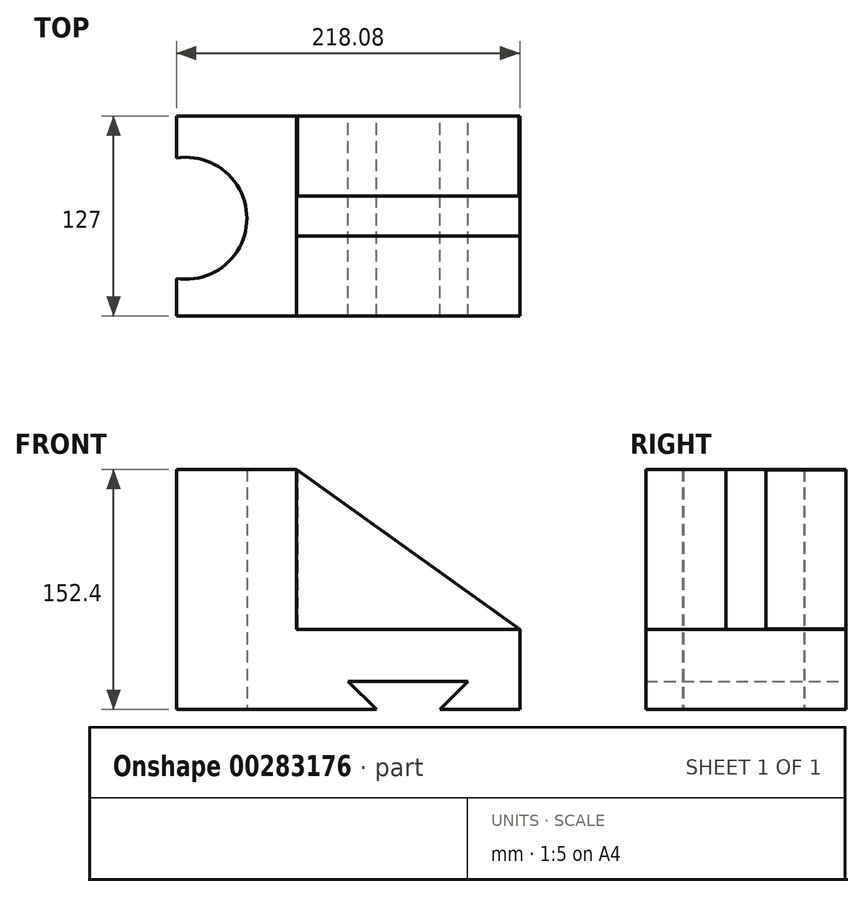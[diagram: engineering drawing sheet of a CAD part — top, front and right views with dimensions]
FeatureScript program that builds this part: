
annotation { "Feature Type Name" : "Feature", "Feature Type Description" : "" }
export const myFeature = defineFeature(function(context is Context, id is Id, definition is map)
    precondition{}
    {
        {
            var Q0;
            Q0=qCreatedBy(makeId("Front.planeOp"),FACE);
            var sketch = newSketch(context, id + "F0", { "sketchPlane" : qUnion([Q0])});
            skLineSegment(sketch, "E0", {"start": v(-163.44, 77.73) * mm, "end": v(-239.64, 77.73) * mm});
            skLineSegment(sketch, "E1", {"start": v(-239.64, 77.73) * mm, "end": v(-239.64, -74.67) * mm});
            skLineSegment(sketch, "E2", {"start": v(-239.64, -74.67) * mm, "end": v(-112.64, -74.67) * mm});
            skLineSegment(sketch, "E3", {"start": v(-112.64, -74.67) * mm, "end": v(-130.6, -56.7) * mm});
            skLineSegment(sketch, "E4", {"start": v(-130.6, -56.7) * mm, "end": v(-54.4, -56.7) * mm});
            skLineSegment(sketch, "E5", {"start": v(-54.4, -56.7) * mm, "end": v(-72.36, -74.67) * mm});
            skLineSegment(sketch, "E6", {"start": v(-72.36, -74.67) * mm, "end": v(-21.56, -74.67) * mm});
            skLineSegment(sketch, "E7", {"start": v(-21.56, -74.67) * mm, "end": v(-21.56, -23.87) * mm});
            skLineSegment(sketch, "E8", {"start": v(-21.56, -23.87) * mm, "end": v(-163.8, -23.87) * mm});
            skLineSegment(sketch, "E9", {"start": v(-163.8, -23.87) * mm, "end": v(-163.44, 77.73) * mm});
            skLineSegment(sketch, "E10", {"start": v(-163.44, 77.73) * mm, "end": v(-21.56, -23.87) * mm});
            skSolve(sketch);
        }
        {
            var Q0;
            Q0=makeQuery(id+"F0.imprint","IMPRINT",FACE,{"disambiguationData":[TD([[makeQuery(id+"F0.imprint","IMPRINT",EDGE,{"derivedFrom":sQuery(id+"F0.wireOp",EDGE,"E0")}),1.0]])]});
            extrude(context, id + "F1", {"entities" : qUnion([Q0]), "depth" : 127 * mm});
        }
        {
            var Q0;
            Q0=qCreatedBy(makeId("Top.planeOp"),FACE);
            var sketch = newSketch(context, id + "F2", { "sketchPlane" : qUnion([Q0])});
            skCircle(sketch, "E11", {"center": v(-233.67, -64.92) * mm, "radius": 38.73 * mm});
            skPoint(sketch, "E11.first.point", {"position": v(-239.98, -26.7) * mm});
            skPoint(sketch, "E11.second.point", {"position": v(-195, -66.9) * mm});
            skPoint(sketch, "E11.third.point", {"position": v(-239.98, -103.13) * mm});
            skSolve(sketch);
        }
        {
            var Q0;
            Q0 = qSketchRegion(id + "F2", true);
            extrude(context, id + "F3", {"entities" : qUnion([Q0]), "operationType" : NewBodyOperationType.REMOVE, "depth" : 127 * mm});
        }
        {
            var Q0;
            Q0=makeQuery(id+"F3.boolean.opBoolean","COPY",FACE,{"derivedFrom":makeQuery(id+"F3.opExtrude","CAP_FACE",FACE,{"disambiguationData":[OSD([sQuery(id+"F2.wireOp",EDGE,"E11")])],"isStart":true})});
            extrude(context, id + "F4", {"entities" : qUnion([Q0]), "operationType" : NewBodyOperationType.REMOVE, "oppositeDirection" : true, "depth" : 127 * mm});
        }
        {
            var Q0;
            Q0=makeQuery(id+"F0.imprint","IMPRINT",FACE,{"disambiguationData":[TD([[makeQuery(id+"F0.imprint","IMPRINT",EDGE,{"derivedFrom":sQuery(id+"F0.wireOp",EDGE,"E8")}),-1.0]])]});
            extrude(context, id + "F5", {"entities" : qUnion([Q0]), "operationType" : NewBodyOperationType.ADD, "depth" : 127 * mm});
        }
        {
            var Q0;
            {var subQ0=sQuery(id+"F0.wireOp",EDGE,"E9");var subQ1=sQuery(id+"F0.wireOp",EDGE,"E8");Q0=makeQuery(id+"F5.boolean.opBoolean","MERGE",FACE,{"derivedFrom":[makeQuery(id+"F1.opExtrude","CAP_FACE",FACE,{"disambiguationData":[OSD([sQuery(id+"F0.wireOp",EDGE,"E0"),sQuery(id+"F0.wireOp",EDGE,"E1"),sQuery(id+"F0.wireOp",EDGE,"E2"),sQuery(id+"F0.wireOp",EDGE,"E3"),sQuery(id+"F0.wireOp",EDGE,"E4"),sQuery(id+"F0.wireOp",EDGE,"E5"),sQuery(id+"F0.wireOp",EDGE,"E6"),sQuery(id+"F0.wireOp",EDGE,"E7"),subQ1,subQ0])],"isStart":false}),makeQuery(id+"F5.opExtrude","CAP_FACE",FACE,{"disambiguationData":[OSD([subQ1,subQ0,sQuery(id+"F0.wireOp",EDGE,"E10")])],"isStart":false})]});}
            var sketch = newSketch(context, id + "F6", { "sketchPlane" : qUnion([Q0])});
            skLineSegment(sketch, "E12", {"start": v(-163.44, 77.73) * mm, "end": v(-163.44, -23.87) * mm});
            skLineSegment(sketch, "E13", {"start": v(-163.44, -23.87) * mm, "end": v(-21.56, -23.87) * mm});
            skLineSegment(sketch, "E14", {"start": v(-21.56, -23.87) * mm, "end": v(-163.44, 77.73) * mm});
            skSolve(sketch);
        }
        {
            var Q0;
            Q0=makeQuery(id+"F6.imprint","IMPRINT",FACE,{"disambiguationData":[TD([[makeQuery(id+"F6.imprint","IMPRINT",EDGE,{"derivedFrom":sQuery(id+"F6.wireOp",EDGE,"E12")}),1.0]])]});
            extrude(context, id + "F7", {"entities" : qUnion([Q0]), "operationType" : NewBodyOperationType.REMOVE, "oppositeDirection" : true, "depth" : 50.8 * mm});
        }
        {
            var Q0;
            Q0=makeQuery(id+"F0.imprint","IMPRINT",FACE,{"disambiguationData":[TD([[makeQuery(id+"F0.imprint","IMPRINT",EDGE,{"derivedFrom":sQuery(id+"F0.wireOp",EDGE,"E0")}),1.0]])]});
            var sketch = newSketch(context, id + "F8", { "sketchPlane" : qUnion([Q0])});
            skLineSegment(sketch, "E15", {"start": v(-20.42, -23.5) * mm, "end": v(-162.88, 78.05) * mm});
            skLineSegment(sketch, "E16", {"start": v(-162.88, 78.05) * mm, "end": v(-162.88, -23.5) * mm});
            skLineSegment(sketch, "E17", {"start": v(-162.88, -23.5) * mm, "end": v(-20.42, -23.5) * mm});
            skSolve(sketch);
        }
        {
            var Q0;
            Q0 = qSketchRegion(id + "F8", true);
            extrude(context, id + "F9", {"entities" : qUnion([Q0]), "operationType" : NewBodyOperationType.REMOVE, "depth" : 50.8 * mm});
        }
    });
